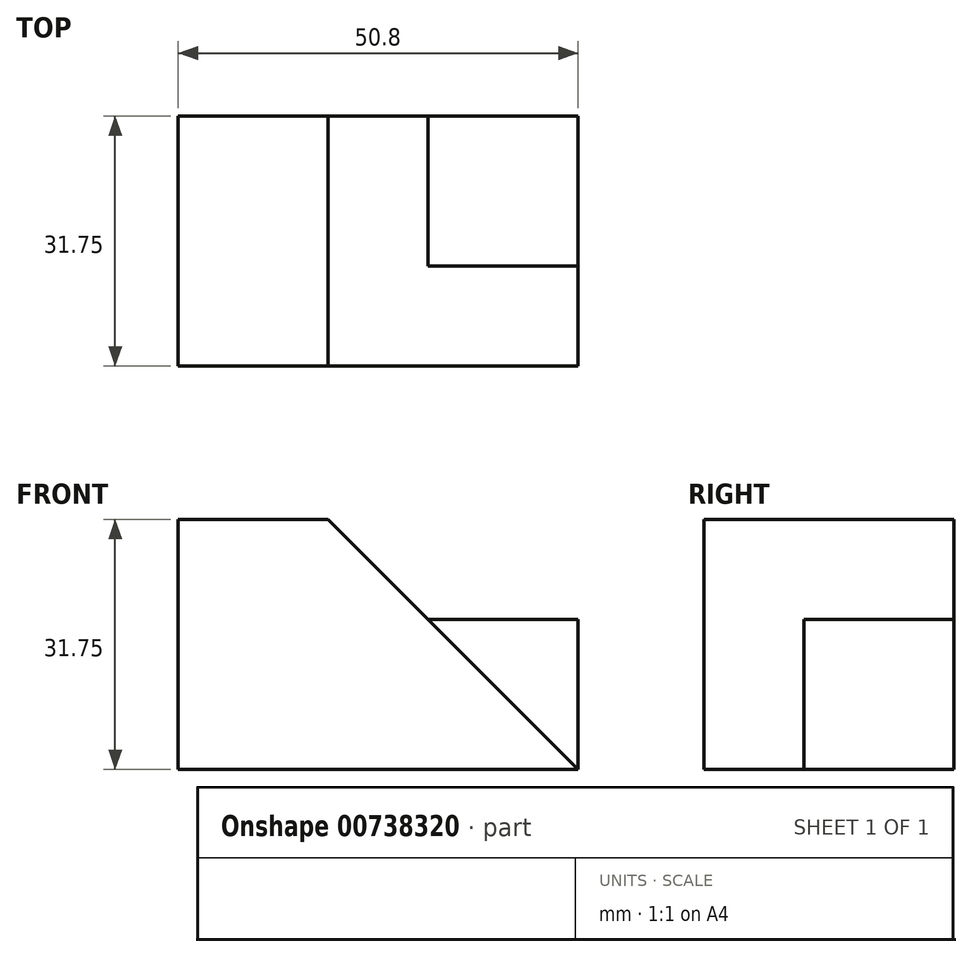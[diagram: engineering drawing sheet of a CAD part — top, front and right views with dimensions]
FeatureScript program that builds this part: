
annotation { "Feature Type Name" : "Feature", "Feature Type Description" : "" }
export const myFeature = defineFeature(function(context is Context, id is Id, definition is map)
    precondition{}
    {
        {
            var Q0;
            Q0=qCreatedBy(makeId("Front.planeOp"),FACE);
            var sketch = newSketch(context, id + "F0", { "sketchPlane" : qUnion([Q0])});
            skLineSegment(sketch, "E0", {"start": v(0, 0) * mm, "end": v(0, 31.75) * mm});
            skLineSegment(sketch, "E1", {"start": v(0, 31.75) * mm, "end": v(19.05, 31.75) * mm});
            skLineSegment(sketch, "E2", {"start": v(19.05, 31.75) * mm, "end": v(50.8, 0) * mm});
            skLineSegment(sketch, "E3", {"start": v(50.8, 0) * mm, "end": v(0, 0) * mm});
            skSolve(sketch);
        }
        {
            var Q0;
            Q0=makeQuery(id+"F0.imprint","IMPRINT",FACE,{"disambiguationData":[TD([[makeQuery(id+"F0.imprint","IMPRINT",EDGE,{"derivedFrom":sQuery(id+"F0.wireOp",EDGE,"E0")}),-1.0]])]});
            extrude(context, id + "F1", {"entities" : qUnion([Q0]), "depth" : 31.75 * mm, "offsetDistance" : 25.4 * mm});
        }
        {
            var Q0;
            Q0=makeQuery(id+"F1.opExtrude","CAP_FACE",FACE,{"disambiguationData":[OSD([sQuery(id+"F0.wireOp",EDGE,"E0"),sQuery(id+"F0.wireOp",EDGE,"E1"),sQuery(id+"F0.wireOp",EDGE,"E2"),sQuery(id+"F0.wireOp",EDGE,"E3")])],"isStart":true});
            var sketch = newSketch(context, id + "F2", { "sketchPlane" : qUnion([Q0])});
            skLineSegment(sketch, "E4", {"start": v(-50.8, 0) * mm, "end": v(-50.8, 19.05) * mm});
            skLineSegment(sketch, "E5", {"start": v(-50.8, 19.05) * mm, "end": v(-31.75, 19.05) * mm});
            skSolve(sketch);
        }
        {
            var Q0;
            {var subQ0=sQuery(id+"F2.wireOp",EDGE,"E4");Q0=makeQuery(id+"F2.imprint","IMPRINT",FACE,{"disambiguationData":[TD([[makeQuery(id+"F2.imprint","IMPRINT",EDGE,{"derivedFrom":subQ0}),-1.0]])]});}
            extrude(context, id + "F3", {"entities" : qUnion([Q0]), "oppositeDirection" : true, "depth" : 19.05 * mm, "offsetDistance" : 25.4 * mm});
        }
    });
